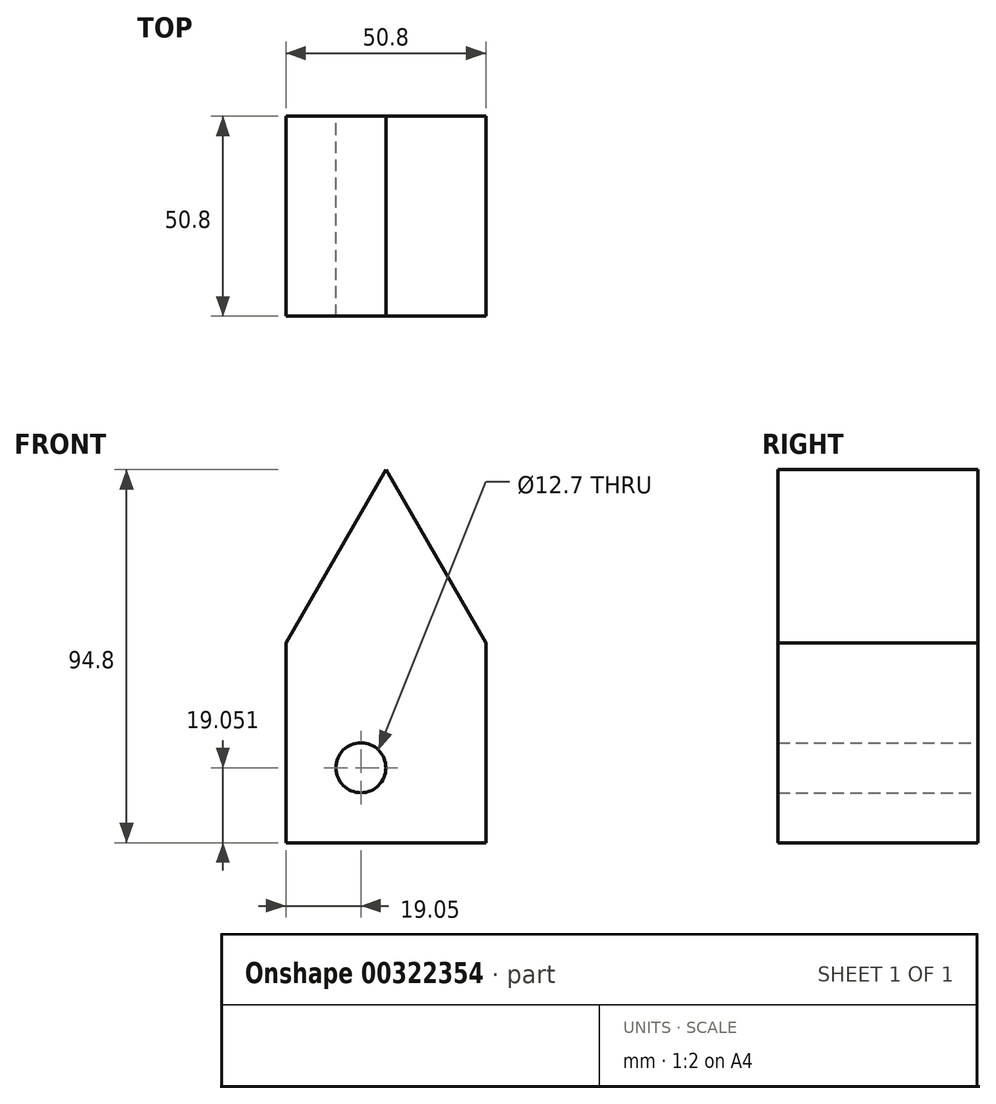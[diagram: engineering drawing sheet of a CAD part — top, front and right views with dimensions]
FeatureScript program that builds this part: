
annotation { "Feature Type Name" : "Feature", "Feature Type Description" : "" }
export const myFeature = defineFeature(function(context is Context, id is Id, definition is map)
    precondition{}
    {
        {
            var Q0;
            Q0=qCreatedBy(makeId("Front.planeOp"),FACE);
            var sketch = newSketch(context, id + "F0", { "sketchPlane" : qUnion([Q0])});
            skLineSegment(sketch, "E0.left", {"start": v(25.4, -33.28) * mm, "end": v(25.4, 17.52) * mm});
            skLineSegment(sketch, "E0.right", {"start": v(-25.4, -33.28) * mm, "end": v(-25.4, 17.52) * mm});
            skLineSegment(sketch, "E1", {"start": v(-25.4, -33.28) * mm, "end": v(25.4, -33.28) * mm});
            skPoint(sketch, "E2.orphan", {"position": v(0, 61.52) * mm});
            skLineSegment(sketch, "E3", {"start": v(0, 61.52) * mm, "end": v(-25.4, 17.52) * mm});
            skLineSegment(sketch, "E4", {"start": v(0, 61.52) * mm, "end": v(25.4, 17.52) * mm});
            skCircle(sketch, "E5", {"center": v(-6.35, -14.23) * mm, "radius": 6.35 * mm});
            skSolve(sketch);
        }
        {
            var Q0;
            Q0=makeQuery(id+"F0.imprint","IMPRINT",FACE,{"disambiguationData":[TD([[makeQuery(id+"F0.imprint","IMPRINT",EDGE,{"derivedFrom":sQuery(id+"F0.wireOp",EDGE,"E0.left")}),1.0]])]});
            extrude(context, id + "F1", {"entities" : qUnion([Q0]), "depth" : 50.8 * mm});
        }
    });
